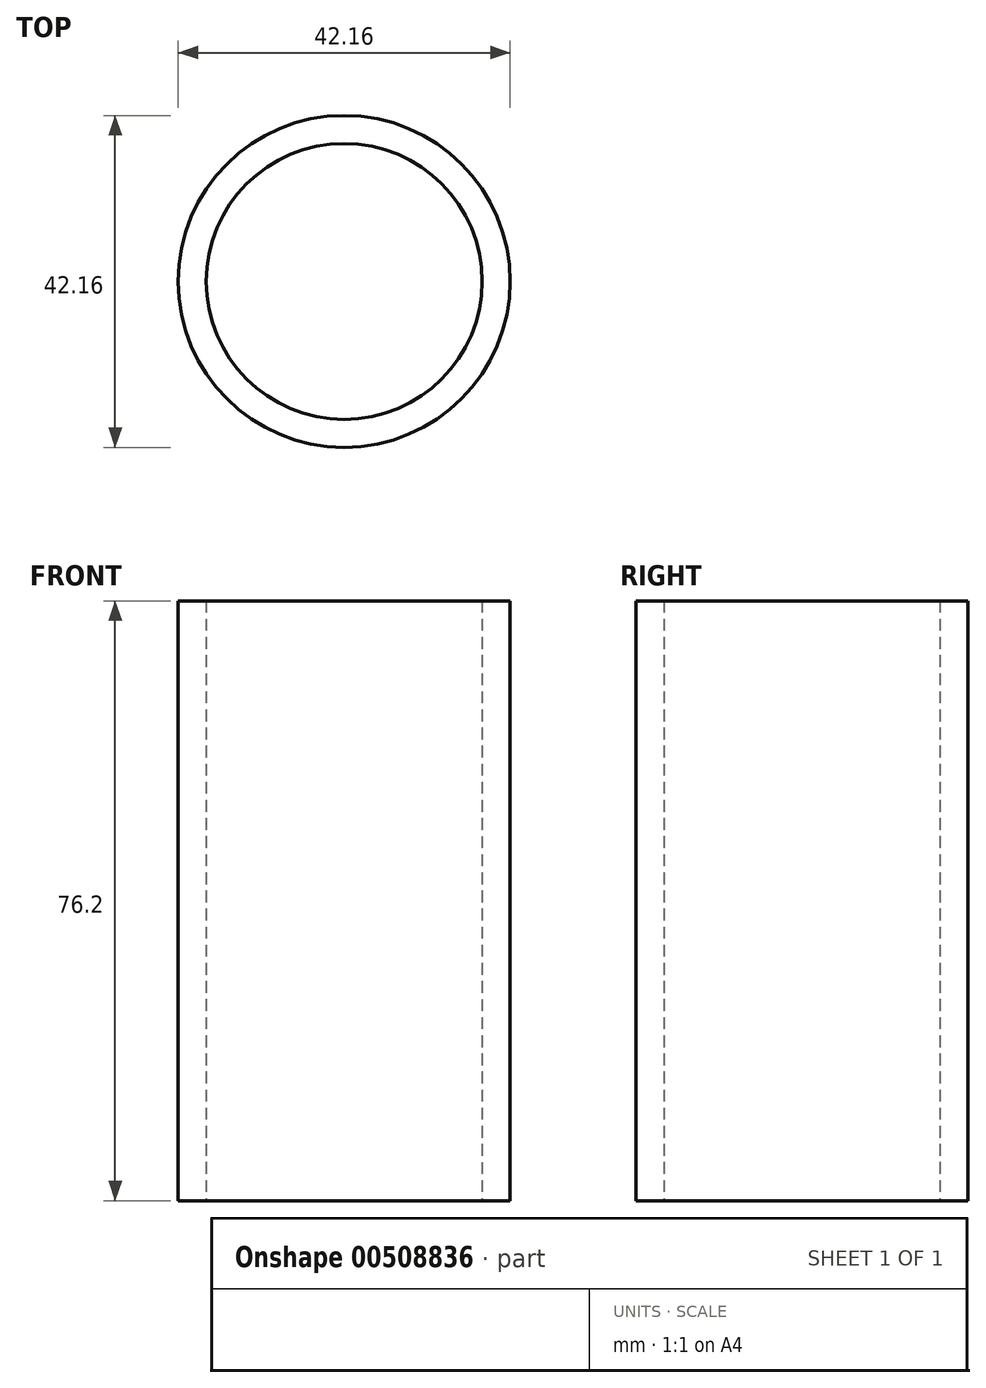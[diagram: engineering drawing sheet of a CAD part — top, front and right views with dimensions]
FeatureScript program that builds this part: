
annotation { "Feature Type Name" : "Feature", "Feature Type Description" : "" }
export const myFeature = defineFeature(function(context is Context, id is Id, definition is map)
    precondition{}
    {
        {
            var Q0;
            Q0=qCreatedBy(makeId("Top.planeOp"),FACE);
            var sketch = newSketch(context, id + "F0", { "sketchPlane" : qUnion([Q0])});
            skCircle(sketch, "E0", {"center": v(0, 0) * mm, "radius": 21.08 * mm});
            skCircle(sketch, "E1", {"center": v(0, 0) * mm, "radius": 17.53 * mm});
            skSolve(sketch);
        }
        {
            var Q0;
            Q0=makeQuery(id+"F0.imprint","IMPRINT",FACE,{"disambiguationData":[TD([[makeQuery(id+"F0.imprint","IMPRINT",EDGE,{"derivedFrom":sQuery(id+"F0.wireOp",EDGE,"E0")}),1.0]])]});
            extrude(context, id + "F1", {"entities" : qUnion([Q0]), "depth" : 76.2 * mm});
        }
    });
